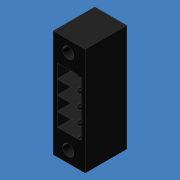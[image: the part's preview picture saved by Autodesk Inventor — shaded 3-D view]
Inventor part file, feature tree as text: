
AUTODESK INVENTOR PART (.ipt)
format: ipt  version: unknown  size: 230,912 bytes
history: native  units: mm (DEFAULTED — no unit token found)
features: sketch x3, extrude x2, hole x1, mirror x1, pattern_linear x1
ambient origin geometry x8: Origin, YZ Plane, XZ Plane, XY Plane, X Axis, Y Axis, Z Axis, Center Point
feature tree (8):
  extrude  "Extrusion1"  Depth=24.2316mm
  hole  "Hole1"  [1 undecoded]
  mirror  "Mirror1"
  extrude  "Extrusion2"  Depth=3.048mm
  pattern_linear  "Rectangular Pattern1"  Spacing1=5.334mm  [1 undecoded]
  sketch  "Sketch1"  dims[d0=7.239mm d1=24.2316mm]
  sketch  "Sketch2"  dims[d2=9.398mm d3=0.0mm d4=9.525mm]
  sketch  "Sketch3"  dims[d5=2.54mm d6=12.7mm d7=9.525mm d8=6.35mm d9=14.3117mm d10=6.35mm d11=20.594885mm d12=3.048mm d13=5.334mm d14=4.572mm d16=2.032mm d17=2.794mm d18=0.508mm d19=5.8293mm d20=6.35mm d21=0.0mm d22=3.429mm d23=40.0mm d25=3.175mm]
note: 2 required parameter values undecoded (feature->parameter linkage not recoverable at this tier; creation-order binding heuristic only, values carry confidence <= 0.55)
